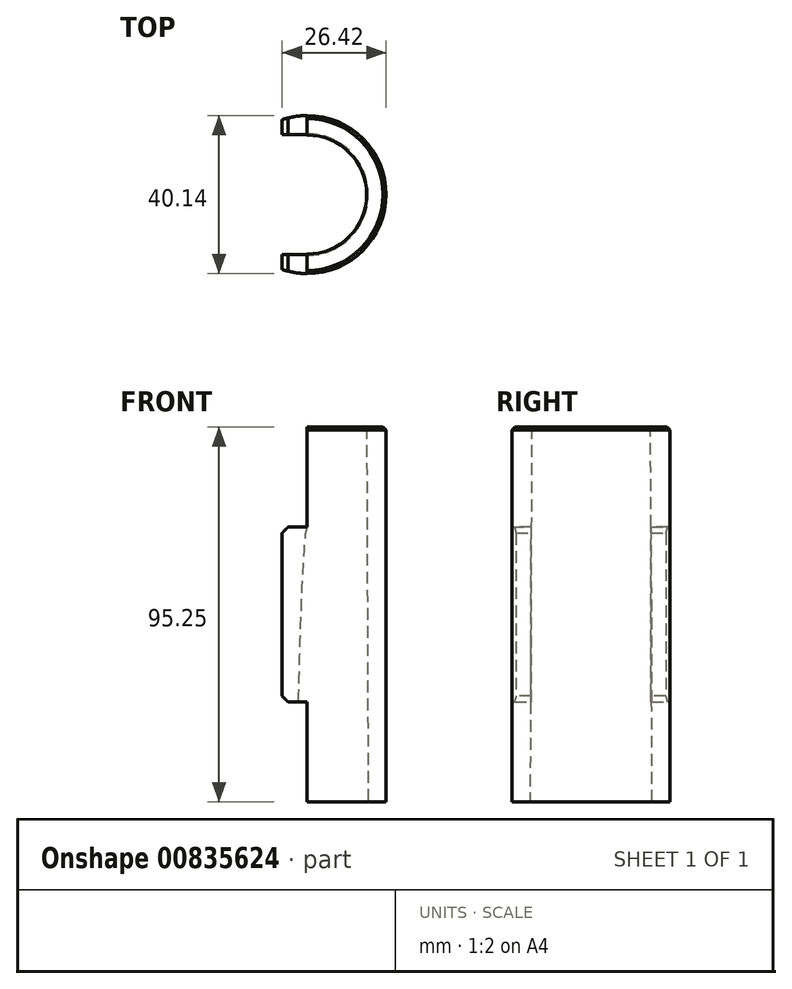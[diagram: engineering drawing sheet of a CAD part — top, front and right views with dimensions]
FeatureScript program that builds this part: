
annotation { "Feature Type Name" : "Feature", "Feature Type Description" : "" }
export const myFeature = defineFeature(function(context is Context, id is Id, definition is map)
    precondition{}
    {
        {
            var Q0;
            Q0=qCreatedBy(makeId("Top.planeOp"),FACE);
            var sketch = newSketch(context, id + "F0", { "sketchPlane" : qUnion([Q0])});
            skCircle(sketch, "E0", {"center": v(0, 0) * mm, "radius": 20.07 * mm});
            skSolve(sketch);
        }
        {
            var Q0;
            Q0 = qSketchRegion(id + "F0", true);
            extrude(context, id + "F1", {"entities" : qUnion([Q0]), "depth" : 95.25 * mm, "offsetDistance" : 25.4 * mm});
        }
        {
            var Q0;
            Q0=qCreatedBy(makeId("Front.planeOp"),FACE);
            var sketch = newSketch(context, id + "F2", { "sketchPlane" : qUnion([Q0])});
            skLineSegment(sketch, "E1", {"start": v(0, 95.25) * mm, "end": v(15.11, 95.25) * mm});
            skLineSegment(sketch, "E2", {"start": v(0, 0) * mm, "end": v(15.5, 0) * mm});
            skLineSegment(sketch, "E3", {"start": v(15.5, 0) * mm, "end": v(15.11, 95.25) * mm});
            skLineSegment(sketch, "E4", {"start": v(0, 95.25) * mm, "end": v(0, 0) * mm});
            skSolve(sketch);
        }
        {
            var Q0;
            Q0 = qSketchRegion(id + "F2", true);
            var Q1;
            Q1=sQuery(id+"F2.wireOp",EDGE,"E4");
            revolve(context, id + "F3", {"operationType" : NewBodyOperationType.REMOVE, "surfaceOperationType" : NewSurfaceOperationType.NEW, "entities" : qUnion([Q0]), "axis" : qUnion([Q1]), "revolveType" : RevolveType.FULL, "oppositeDirection" : true});
        }
        {
            var Q0;
            Q0=qCreatedBy(makeId("Front.planeOp"),FACE);
            var sketch = newSketch(context, id + "F4", { "sketchPlane" : qUnion([Q0])});
            skLineSegment(sketch, "E5", {"start": v(0, 95.25) * mm, "end": v(0, 69.85) * mm});
            skLineSegment(sketch, "E6", {"start": v(0, 69.85) * mm, "end": v(-6.35, 69.85) * mm});
            skLineSegment(sketch, "E7", {"start": v(-6.35, 69.85) * mm, "end": v(-6.35, 25.4) * mm});
            skLineSegment(sketch, "E8", {"start": v(-6.35, 25.4) * mm, "end": v(0, 25.4) * mm});
            skLineSegment(sketch, "E9", {"start": v(0, 25.4) * mm, "end": v(0, 0) * mm});
            skLineSegment(sketch, "E10", {"start": v(0, 95.25) * mm, "end": v(-20.56, 95.25) * mm});
            skLineSegment(sketch, "E11", {"start": v(-20.56, 95.25) * mm, "end": v(-20.56, 0) * mm});
            skLineSegment(sketch, "E12", {"start": v(-20.56, 0) * mm, "end": v(0, 0) * mm});
            skSolve(sketch);
        }
        {
            var Q0;
            Q0 = qSketchRegion(id + "F4", true);
            extrude(context, id + "F5", {"entities" : qUnion([Q0]), "operationType" : NewBodyOperationType.REMOVE, "endBound" : BoundingType.THROUGH_ALL, "depth" : 25.4 * mm, "offsetDistance" : 25.4 * mm, "hasSecondDirection" : true, "secondDirectionOppositeDirection" : true, "secondDirectionDepth" : 50.8 * mm});
        }
        {
            var Q0;
            Q0=makeQuery(id+"F1.opExtrude","CAP_FACE",FACE,{"disambiguationData":[OSD([sQuery(id+"F0.wireOp",EDGE,"E0")])],"isStart":false});
            var sketch = newSketch(context, id + "F6", { "sketchPlane" : qUnion([Q0])});
            skLineSegment(sketch, "E13", {"start": v(0, -15.21) * mm, "end": v(-6.35, -15.21) * mm});
            skArc(sketch, "E14.1.1", {"start": v(-6.35, -13.83) * mm, "mid": v(-3.25, -14.86) * mm, "end": v(0, -15.21) * mm});
            skLineSegment(sketch, "E14.1.2", {"start": v(-6.35, -13.83) * mm, "end": v(-6.35, -15.21) * mm});
            skLineSegment(sketch, "E14.2.0", {"start": v(-6.35, 15.21) * mm, "end": v(-6.35, 13.83) * mm});
            skArc(sketch, "E14.2.1", {"start": v(0, 15.21) * mm, "mid": v(-3.25, 14.86) * mm, "end": v(-6.35, 13.83) * mm});
            skPoint(sketch, "E14.1.3.end.orphan", {"position": v(0, -20.07) * mm});
            skPoint(sketch, "E15.orphan", {"position": v(-6.35, -19.03) * mm});
            skLineSegment(sketch, "E16", {"start": v(0, 15.21) * mm, "end": v(-6.35, 15.21) * mm});
            skPoint(sketch, "E14.2.3.end.orphan", {"position": v(-6.35, 19.03) * mm});
            skPoint(sketch, "E14.2.2.end.orphan", {"position": v(0, 20.07) * mm});
            skSolve(sketch);
        }
        {
            var Q0;
            Q0 = qSketchRegion(id + "F6", true);
            extrude(context, id + "F7", {"entities" : qUnion([Q0]), "operationType" : NewBodyOperationType.REMOVE, "endBound" : BoundingType.THROUGH_ALL, "oppositeDirection" : true, "depth" : 25.4 * mm, "offsetDistance" : 25.4 * mm});
        }
        {
            var Q0;
            Q0=makeQuery(id+"F5.boolean.opBoolean","COPY",EDGE,{"disambiguationData":[OD(1.0)],"derivedFrom":makeQuery(id+"F5.opExtrude","SWEPT_EDGE",EDGE,{"disambiguationData":[OSD([sQuery(id+"F4.wireOp",EDGE,"E6"),sQuery(id+"F4.wireOp",EDGE,"E7")])]})});
            var Q1;
            Q1=makeQuery(id+"F5.boolean.opBoolean","COPY",EDGE,{"disambiguationData":[OD(0.0)],"derivedFrom":makeQuery(id+"F5.opExtrude","SWEPT_EDGE",EDGE,{"disambiguationData":[OSD([sQuery(id+"F4.wireOp",EDGE,"E6"),sQuery(id+"F4.wireOp",EDGE,"E7")])]})});
            var Q2;
            Q2=makeQuery(id+"F5.boolean.opBoolean","COPY",EDGE,{"disambiguationData":[OD(1.0)],"derivedFrom":makeQuery(id+"F5.opExtrude","SWEPT_EDGE",EDGE,{"disambiguationData":[OSD([sQuery(id+"F4.wireOp",EDGE,"E7"),sQuery(id+"F4.wireOp",EDGE,"E8")])]})});
            var Q3;
            Q3=makeQuery(id+"F5.boolean.opBoolean","COPY",EDGE,{"disambiguationData":[OD(0.0)],"derivedFrom":makeQuery(id+"F5.opExtrude","SWEPT_EDGE",EDGE,{"disambiguationData":[OSD([sQuery(id+"F4.wireOp",EDGE,"E7"),sQuery(id+"F4.wireOp",EDGE,"E8")])]})});
            chamfer(context, id + "F8", {"entities" : qUnion([Q0, Q1, Q2, Q3]), "width" : 1.52 * mm, "tangentPropagation" : true});
        }
        {
            var Q0;
            Q0=makeQuery(id+"F3.boolean.opBoolean","COPY",EDGE,{"derivedFrom":makeQuery(id+"F3.opRevolve","SWEPT_EDGE",EDGE,{"disambiguationData":[OSD([sQuery(id+"F2.wireOp",EDGE,"E1"),sQuery(id+"F2.wireOp",EDGE,"E3")])]})});
            var Q1;
            Q1=makeQuery(id+"F1.opExtrude","CAP_EDGE",EDGE,{"disambiguationData":[OSD([sQuery(id+"F0.wireOp",EDGE,"E0")])],"isStart":false});
            var Q2;
            Q2=makeQuery(id+"F5.boolean.opBoolean","COPY",EDGE,{"disambiguationData":[OD(0.0)],"derivedFrom":makeQuery(id+"F5.opExtrude","SWEPT_EDGE",EDGE,{"disambiguationData":[OSD([sQuery(id+"F4.wireOp",EDGE,"E5"),sQuery(id+"F4.wireOp",EDGE,"E10")])]})});
            var Q3;
            Q3=makeQuery(id+"F5.boolean.opBoolean","COPY",EDGE,{"disambiguationData":[OD(1.0)],"derivedFrom":makeQuery(id+"F5.opExtrude","SWEPT_EDGE",EDGE,{"disambiguationData":[OSD([sQuery(id+"F4.wireOp",EDGE,"E5"),sQuery(id+"F4.wireOp",EDGE,"E10")])]})});
            chamfer(context, id + "F9", {"entities" : qUnion([Q0, Q1, Q2, Q3]), "width" : 0.76 * mm, "tangentPropagation" : true});
        }
    });
